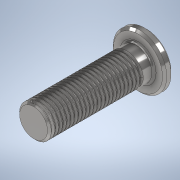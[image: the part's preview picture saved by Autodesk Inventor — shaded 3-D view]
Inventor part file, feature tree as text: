
AUTODESK INVENTOR PART (.ipt)
format: ipt  version: 2021 (Build 250183000, 183)  size: 699,392 bytes
history: native  units: in
note: dims shown in document units (in); Inventor stores cm internally (conversion verified against a paired STEP export)
features: sketch x5, extrude x4, chamfer x3, fillet x2, helix x1, projected_geometry x1
ambient origin geometry x8: Origin, YZ Plane, XZ Plane, XY Plane, X Axis, Y Axis, Z Axis, Center Point
bodies: Solid2 (feature_tree)
feature tree (16):
  extrude  "Extrusion3"  Depth=0.1917in TaperAngle=0.0deg
  chamfer  "Chamfer1"  Distance=0.0039in Angle=45.0deg
  extrude  "Extrusion4"  Depth=0.0157in TaperAngle=0.0deg
  fillet  "Fillet1"  Radius=0.0039in
  chamfer  "Chamfer2"  Distance=0.0039in Angle=45.0deg
  chamfer  "Chamfer3"  Distance=0.0039in Angle=45.0deg
  extrude  "Extrusion5"  Depth=0.0118in
  helix  "Coil1"  [1 undecoded]
  fillet  "Fillet3"  Radius=0.0591in
  extrude  "Extrusion6"  TaperAngle=60.0deg  [1 undecoded]
  sketch  "Sketch3"  dims[d6=0.0591in d7=0.1917in d8=0.0in d9=0.0039in d10=0.0787in d11=45.0deg]
  sketch  "Sketch4"  dims[d12=0.0984in d13=0.0157in d14=0.0in d15=0.0039in d17=0.0039in d18=0.0787in d19=45.0deg d20=0.0039in d21=0.0787in d22=45.0deg]
  sketch  "Sketch5"  dims[d23=0.0079in d24=0.0in d25=0.0118in d26=0.0118in d27=0.0591in]
  sketch  "Sketch6"  dims[d32=0.0197in d33=60.0deg]
  sketch  "Sketch7"  dims[d35=0.0039in d36=0.002in d37=0.0071in d38=0.3937in d39=9.1732in d40=0.0in d41=90.0deg d42=90.0deg d43=0.0in d44=0.0in d45=0.0039in d46=0.0236in d47=0.0in]
  projected_geometry  "Projected Loop1"
note: 2 required parameter values undecoded (feature->parameter linkage not recoverable at this tier; creation-order binding heuristic only, values carry confidence <= 0.55)
